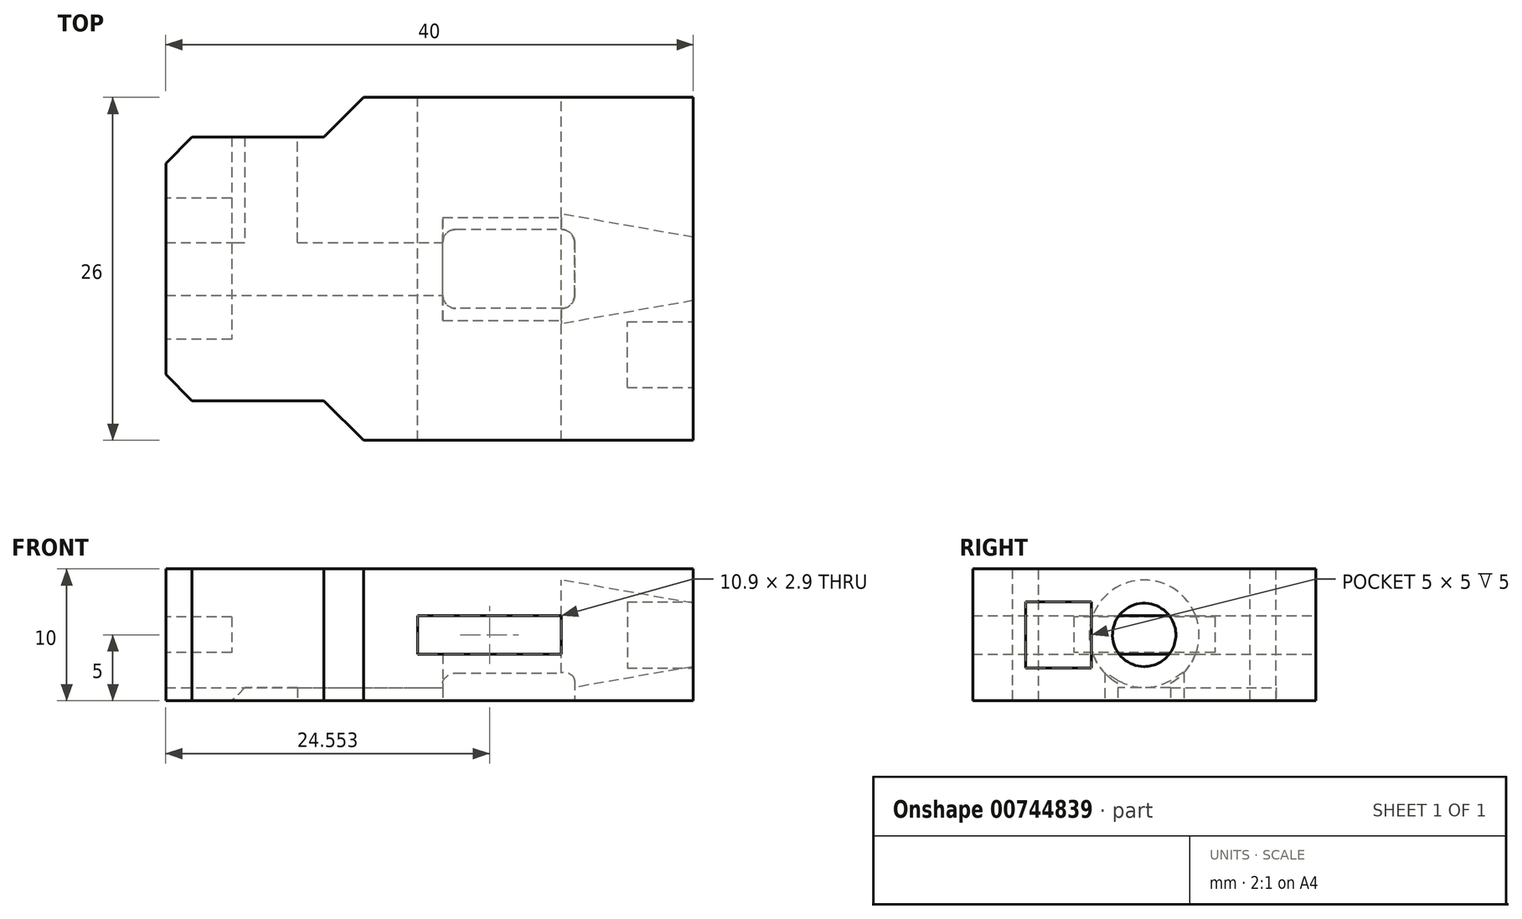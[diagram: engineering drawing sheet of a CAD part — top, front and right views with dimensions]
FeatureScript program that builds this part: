
annotation { "Feature Type Name" : "Feature", "Feature Type Description" : "" }
export const myFeature = defineFeature(function(context is Context, id is Id, definition is map)
    precondition{}
    {
        {
            var Q0;
            Q0=qCreatedBy(makeId("Top.planeOp"),FACE);
            var sketch = newSketch(context, id + "F0", { "sketchPlane" : qUnion([Q0])});
            skPoint(sketch, "E0", {"position": v(-7.73, 0) * mm});
            skLineSegment(sketch, "E1.bottom", {"start": v(-2.73, 10) * mm, "end": v(-12.73, 10) * mm});
            skLineSegment(sketch, "E1.top", {"start": v(-2.73, -10) * mm, "end": v(-12.73, -10) * mm});
            skLineSegment(sketch, "E1.left", {"start": v(-2.73, 10) * mm, "end": v(-2.73, -10) * mm});
            skLineSegment(sketch, "E1.right", {"start": v(-12.73, 10) * mm, "end": v(-12.73, -10) * mm});
            skLineSegment(sketch, "E2", {"start": v(-2.73, 10) * mm, "end": v(-2.73, 13) * mm});
            skLineSegment(sketch, "E3", {"start": v(-2.73, 13) * mm, "end": v(27.27, 13) * mm});
            skLineSegment(sketch, "E4", {"start": v(27.27, 13) * mm, "end": v(27.27, -13) * mm});
            skLineSegment(sketch, "E5", {"start": v(27.27, -13) * mm, "end": v(-2.73, -13) * mm});
            skLineSegment(sketch, "E6", {"start": v(-2.73, -13) * mm, "end": v(-2.73, -10) * mm});
            skSolve(sketch);
        }
        {
            var Q0;
            Q0=makeQuery(id+"F0.imprint","IMPRINT",FACE,{"disambiguationData":[TD([[makeQuery(id+"F0.imprint","IMPRINT",EDGE,{"derivedFrom":sQuery(id+"F0.wireOp",EDGE,"E1.bottom")}),1.0]])]});
            var Q1;
            Q1=makeQuery(id+"F0.imprint","IMPRINT",FACE,{"disambiguationData":[TD([[makeQuery(id+"F0.imprint","IMPRINT",EDGE,{"derivedFrom":sQuery(id+"F0.wireOp",EDGE,"E1.left")}),1.0]])]});
            extrude(context, id + "F1", {"entities" : qUnion([Q0, Q1]), "depth" : 10 * mm});
        }
        {
            var Q0;
            Q0=makeQuery(id+"F1.opExtrude","SWEPT_FACE",FACE,{"disambiguationData":[OSD([sQuery(id+"F0.wireOp",EDGE,"E1.right")])]});
            var sketch = newSketch(context, id + "F2", { "sketchPlane" : qUnion([Q0])});
            skLineSegment(sketch, "E7", {"start": v(-10, 10) * mm, "end": v(10, 0) * mm});
            skLineSegment(sketch, "E8", {"start": v(-10, 0) * mm, "end": v(10, 10) * mm});
            skLineSegment(sketch, "E9.bottom", {"start": v(-5.35, 6.35) * mm, "end": v(5.35, 6.35) * mm});
            skLineSegment(sketch, "E9.top", {"start": v(-5.35, 3.65) * mm, "end": v(5.35, 3.65) * mm});
            skLineSegment(sketch, "E9.left", {"start": v(-5.35, 6.35) * mm, "end": v(-5.35, 3.65) * mm});
            skLineSegment(sketch, "E9.right", {"start": v(5.35, 6.35) * mm, "end": v(5.35, 3.65) * mm});
            skPoint(sketch, "E9.middle", {"position": v(0, 5) * mm});
            skSolve(sketch);
        }
        {
            var Q0;
            {var subQ0=sQuery(id+"F2.wireOp",EDGE,"E9.left");Q0=makeQuery(id+"F2.imprint","IMPRINT",FACE,{"disambiguationData":[TD([[makeQuery(id+"F2.imprint","IMPRINT",EDGE,{"derivedFrom":subQ0}),1.0]])]});}
            var Q1;
            {var subQ0=sQuery(id+"F2.wireOp",EDGE,"E8");var subQ1=sQuery(id+"F2.wireOp",EDGE,"E7");var subQ2=makeQuery(id+"F2.imprint","INTERSECT",VERTEX,{"derivedFrom":[subQ1,subQ0]});Q1=makeQuery(id+"F2.imprint","IMPRINT",FACE,{"disambiguationData":[TD([[makeQuery(id+"F2.imprint","IMPRINT",EDGE,{"disambiguationData":[TD([[subQ2,-1.0]])],"derivedFrom":subQ1}),-1.0]])]});}
            var Q2;
            {var subQ0=sQuery(id+"F2.wireOp",EDGE,"E9.right");Q2=makeQuery(id+"F2.imprint","IMPRINT",FACE,{"disambiguationData":[TD([[makeQuery(id+"F2.imprint","IMPRINT",EDGE,{"derivedFrom":subQ0}),-1.0]])]});}
            var Q3;
            {var subQ0=sQuery(id+"F2.wireOp",EDGE,"E9.bottom");var subQ1=sQuery(id+"F2.wireOp",EDGE,"E7");var subQ2=makeQuery(id+"F2.imprint","INTERSECT",VERTEX,{"derivedFrom":[subQ1,subQ0]});Q3=makeQuery(id+"F2.imprint","IMPRINT",FACE,{"disambiguationData":[TD([[makeQuery(id+"F2.imprint","IMPRINT",EDGE,{"disambiguationData":[TD([[subQ2,-1.0]])],"derivedFrom":subQ1}),1.0]])]});}
            extrude(context, id + "F3", {"entities" : qUnion([Q0, Q1, Q2, Q3]), "operationType" : NewBodyOperationType.REMOVE, "oppositeDirection" : true, "depth" : 5 * mm});
        }
        {
            var Q0;
            Q0=makeQuery(id+"F1.opExtrude","SWEPT_EDGE",EDGE,{"disambiguationData":[OSD([sQuery(id+"F0.wireOp",EDGE,"E2"),sQuery(id+"F0.wireOp",EDGE,"E3")])]});
            var Q1;
            Q1=makeQuery(id+"F1.opExtrude","SWEPT_EDGE",EDGE,{"disambiguationData":[OSD([sQuery(id+"F0.wireOp",EDGE,"E5"),sQuery(id+"F0.wireOp",EDGE,"E6")])]});
            chamfer(context, id + "F4", {"entities" : qUnion([Q0, Q1]), "width" : 5 * mm, "tangentPropagation" : true});
        }
        {
            var Q0;
            Q0=makeQuery(id+"F1.opExtrude","SWEPT_EDGE",EDGE,{"disambiguationData":[OSD([sQuery(id+"F0.wireOp",EDGE,"E1.bottom"),sQuery(id+"F0.wireOp",EDGE,"E1.right")])]});
            var Q1;
            Q1=makeQuery(id+"F1.opExtrude","SWEPT_EDGE",EDGE,{"disambiguationData":[OSD([sQuery(id+"F0.wireOp",EDGE,"E1.top"),sQuery(id+"F0.wireOp",EDGE,"E1.right")])]});
            chamfer(context, id + "F5", {"entities" : qUnion([Q0, Q1]), "width" : 2 * mm, "tangentPropagation" : true});
        }
        {
            var Q0;
            Q0=makeQuery(id+"F1.opExtrude","SWEPT_FACE",FACE,{"disambiguationData":[OSD([sQuery(id+"F0.wireOp",EDGE,"E3")])]});
            var sketch = newSketch(context, id + "F6", { "sketchPlane" : qUnion([Q0])});
            skLineSegment(sketch, "E10", {"start": v(-27.27, 10) * mm, "end": v(-2.27, 0) * mm});
            skLineSegment(sketch, "E11", {"start": v(-2.27, 0) * mm, "end": v(-2.27, 10) * mm});
            skLineSegment(sketch, "E12", {"start": v(-2.27, 10) * mm, "end": v(-27.27, 0) * mm});
            skLineSegment(sketch, "E13", {"start": v(-14.77, 5) * mm, "end": v(-27.27, 5) * mm});
            skLineSegment(sketch, "E14", {"start": v(-14.77, 5) * mm, "end": v(-2.27, 5) * mm});
            skPoint(sketch, "E15", {"position": v(-17.27, 5) * mm});
            skLineSegment(sketch, "E16", {"start": v(-17.27, 5) * mm, "end": v(-17.27, 6.45) * mm});
            skLineSegment(sketch, "E17", {"start": v(-17.27, 6.45) * mm, "end": v(-6.37, 6.45) * mm});
            skLineSegment(sketch, "E18", {"start": v(-6.37, 6.45) * mm, "end": v(-6.37, 5) * mm});
            skLineSegment(sketch, "E19.MirrorCS", {"start": v(-17.27, 3.55) * mm, "end": v(-6.37, 3.55) * mm});
            skLineSegment(sketch, "E20.MirrorCS", {"start": v(-17.27, 5) * mm, "end": v(-17.27, 3.55) * mm});
            skLineSegment(sketch, "E21.MirrorCS", {"start": v(-6.37, 3.55) * mm, "end": v(-6.37, 5) * mm});
            skSolve(sketch);
        }
        {
            var Q0;
            {var subQ5=sQuery(id+"F6.wireOp",EDGE,"E16");Q0=makeQuery(id+"F6.imprint","IMPRINT",FACE,{"disambiguationData":[TD([[makeQuery(id+"F6.imprint","IMPRINT",EDGE,{"derivedFrom":subQ5}),-1.0]])]});}
            var Q1;
            {var subQ3=sQuery(id+"F6.wireOp",EDGE,"E17");var subQ5=sQuery(id+"F6.wireOp",EDGE,"E18");var subQ6=makeQuery(id+"F6.imprint","INTERSECT",VERTEX,{"derivedFrom":[subQ3,subQ5]});Q1=makeQuery(id+"F6.imprint","IMPRINT",FACE,{"disambiguationData":[TD([[makeQuery(id+"F6.imprint","IMPRINT",EDGE,{"disambiguationData":[TD([[subQ6,1.0]])],"derivedFrom":subQ3}),-1.0]])]});}
            var Q2;
            {var subQ5=sQuery(id+"F6.wireOp",EDGE,"E20.MirrorCS");Q2=makeQuery(id+"F6.imprint","IMPRINT",FACE,{"disambiguationData":[TD([[makeQuery(id+"F6.imprint","IMPRINT",EDGE,{"derivedFrom":subQ5}),1.0]])]});}
            var Q3;
            {var subQ3=sQuery(id+"F6.wireOp",EDGE,"E21.MirrorCS");var subQ5=sQuery(id+"F6.wireOp",EDGE,"E19.MirrorCS");var subQ6=makeQuery(id+"F6.imprint","INTERSECT",VERTEX,{"derivedFrom":[subQ5,subQ3]});Q3=makeQuery(id+"F6.imprint","IMPRINT",FACE,{"disambiguationData":[TD([[makeQuery(id+"F6.imprint","IMPRINT",EDGE,{"disambiguationData":[TD([[subQ6,1.0]])],"derivedFrom":subQ5}),1.0]])]});}
            var Q4;
            {var subQ1=sQuery(id+"F6.wireOp",EDGE,"E12");var subQ3=sQuery(id+"F6.wireOp",EDGE,"E18");var subQ4=makeQuery(id+"F6.imprint","INTERSECT",VERTEX,{"derivedFrom":[subQ1,subQ3]});Q4=makeQuery(id+"F6.imprint","IMPRINT",FACE,{"disambiguationData":[TD([[makeQuery(id+"F6.imprint","IMPRINT",EDGE,{"disambiguationData":[TD([[subQ4,-1.0]])],"derivedFrom":subQ3}),-1.0]])]});}
            var Q5;
            {var subQ1=sQuery(id+"F6.wireOp",EDGE,"E10");var subQ3=sQuery(id+"F6.wireOp",EDGE,"E21.MirrorCS");var subQ4=makeQuery(id+"F6.imprint","INTERSECT",VERTEX,{"derivedFrom":[subQ1,subQ3]});Q5=makeQuery(id+"F6.imprint","IMPRINT",FACE,{"disambiguationData":[TD([[makeQuery(id+"F6.imprint","IMPRINT",EDGE,{"disambiguationData":[TD([[subQ4,-1.0]])],"derivedFrom":subQ3}),1.0]])]});}
            var Q6;
            {var subQ1=sQuery(id+"F6.wireOp",EDGE,"E10");var subQ3=sQuery(id+"F6.wireOp",EDGE,"E19.MirrorCS");var subQ4=makeQuery(id+"F6.imprint","INTERSECT",VERTEX,{"derivedFrom":[subQ1,subQ3]});Q6=makeQuery(id+"F6.imprint","IMPRINT",FACE,{"disambiguationData":[TD([[makeQuery(id+"F6.imprint","IMPRINT",EDGE,{"disambiguationData":[TD([[subQ4,1.0]])],"derivedFrom":subQ3}),1.0]])]});}
            var Q7;
            {var subQ1=sQuery(id+"F6.wireOp",EDGE,"E10");var subQ3=sQuery(id+"F6.wireOp",EDGE,"E17");var subQ4=makeQuery(id+"F6.imprint","INTERSECT",VERTEX,{"derivedFrom":[subQ1,subQ3]});Q7=makeQuery(id+"F6.imprint","IMPRINT",FACE,{"disambiguationData":[TD([[makeQuery(id+"F6.imprint","IMPRINT",EDGE,{"disambiguationData":[TD([[subQ4,-1.0]])],"derivedFrom":subQ3}),-1.0]])]});}
            var Q8;
            Q8=makeQuery(id+"F1.opExtrude","SWEPT_FACE",FACE,{"disambiguationData":[OSD([sQuery(id+"F0.wireOp",EDGE,"E5")])]});
            extrude(context, id + "F7", {"entities" : qUnion([Q0, Q1, Q2, Q3, Q4, Q5, Q6, Q7]), "operationType" : NewBodyOperationType.REMOVE, "endBound" : BoundingType.UP_TO_SURFACE, "oppositeDirection" : true, "endBoundEntityFace" : qUnion([Q8]), "depth" : 25 * mm});
        }
        {
            var Q0;
            Q0=makeQuery(id+"F1.opExtrude","SWEPT_FACE",FACE,{"disambiguationData":[OSD([sQuery(id+"F0.wireOp",EDGE,"E4")])]});
            var sketch = newSketch(context, id + "F8", { "sketchPlane" : qUnion([Q0])});
            skLineSegment(sketch, "E22", {"start": v(13, 0) * mm, "end": v(-13, 10) * mm});
            skLineSegment(sketch, "E23", {"start": v(13, 10) * mm, "end": v(-13, 0) * mm});
            skPoint(sketch, "E24", {"position": v(0, 5) * mm});
            skCircle(sketch, "E25", {"center": v(0, 5) * mm, "radius": 2.4 * mm});
            skLineSegment(sketch, "E26", {"start": v(0, 5) * mm, "end": v(-13, 5) * mm});
            skPoint(sketch, "E27", {"position": v(-6.5, 5) * mm});
            skLineSegment(sketch, "E28.bottom", {"start": v(-9, 7.5) * mm, "end": v(-4, 7.5) * mm});
            skLineSegment(sketch, "E28.top", {"start": v(-9, 2.5) * mm, "end": v(-4, 2.5) * mm});
            skLineSegment(sketch, "E28.left", {"start": v(-9, 7.5) * mm, "end": v(-9, 2.5) * mm});
            skLineSegment(sketch, "E28.right", {"start": v(-4, 7.5) * mm, "end": v(-4, 2.5) * mm});
            skSolve(sketch);
        }
        {
            var Q0;
            {var subQ0=sQuery(id+"F8.wireOp",EDGE,"E23");var subQ1=sQuery(id+"F8.wireOp",EDGE,"E22");var subQ2=makeQuery(id+"F8.imprint","INTERSECT",VERTEX,{"derivedFrom":[subQ1,subQ0]});Q0=makeQuery(id+"F8.imprint","IMPRINT",FACE,{"disambiguationData":[TD([[makeQuery(id+"F8.imprint","IMPRINT",EDGE,{"disambiguationData":[TD([[subQ2,-1.0]])],"derivedFrom":subQ1}),1.0]])]});}
            var Q1;
            {var subQ0=sQuery(id+"F8.wireOp",EDGE,"E23");var subQ1=sQuery(id+"F8.wireOp",EDGE,"E22");var subQ2=makeQuery(id+"F8.imprint","INTERSECT",VERTEX,{"derivedFrom":[subQ1,subQ0]});Q1=makeQuery(id+"F8.imprint","IMPRINT",FACE,{"disambiguationData":[TD([[makeQuery(id+"F8.imprint","IMPRINT",EDGE,{"disambiguationData":[TD([[subQ2,-1.0]])],"derivedFrom":subQ1}),-1.0]])]});}
            var Q2;
            {var subQ0=sQuery(id+"F8.wireOp",EDGE,"E25");var subQ1=sQuery(id+"F8.wireOp",EDGE,"E22");var subQ2=makeQuery(id+"F8.imprint","INTERSECT",VERTEX,{"disambiguationData":[OD(0.0)],"derivedFrom":[subQ1,subQ0]});Q2=makeQuery(id+"F8.imprint","IMPRINT",FACE,{"disambiguationData":[TD([[makeQuery(id+"F8.imprint","IMPRINT",EDGE,{"disambiguationData":[TD([[subQ2,-1.0]])],"derivedFrom":subQ1}),-1.0]])]});}
            var Q3;
            {var subQ0=sQuery(id+"F8.wireOp",EDGE,"E25");var subQ1=sQuery(id+"F8.wireOp",EDGE,"E22");var subQ2=makeQuery(id+"F8.imprint","INTERSECT",VERTEX,{"disambiguationData":[OD(0.0)],"derivedFrom":[subQ1,subQ0]});Q3=makeQuery(id+"F8.imprint","IMPRINT",FACE,{"disambiguationData":[TD([[makeQuery(id+"F8.imprint","IMPRINT",EDGE,{"disambiguationData":[TD([[subQ2,-1.0]])],"derivedFrom":subQ1}),1.0]])]});}
            var Q4;
            {var subQ1=sQuery(id+"F8.wireOp",EDGE,"E23");var subQ3=sQuery(id+"F8.wireOp",EDGE,"E25");var subQ4=makeQuery(id+"F8.imprint","INTERSECT",VERTEX,{"disambiguationData":[OD(1.0)],"derivedFrom":[subQ1,subQ3]});Q4=makeQuery(id+"F8.imprint","IMPRINT",FACE,{"disambiguationData":[TD([[makeQuery(id+"F8.imprint","IMPRINT",EDGE,{"disambiguationData":[TD([[subQ4,1.0]])],"derivedFrom":subQ3}),1.0]])]});}
            var Q5;
            Q5=makeQuery(id+"F7.boolean.opBoolean","COPY",FACE,{"derivedFrom":makeQuery(id+"F7.opExtrude","SWEPT_FACE",FACE,{"disambiguationData":[OSD([sQuery(id+"F6.wireOp",EDGE,"E16"),sQuery(id+"F6.wireOp",EDGE,"E20.MirrorCS")])]})});
            extrude(context, id + "F9", {"entities" : qUnion([Q0, Q1, Q2, Q3, Q4]), "operationType" : NewBodyOperationType.REMOVE, "endBound" : BoundingType.UP_TO_SURFACE, "oppositeDirection" : true, "endBoundEntityFace" : qUnion([Q5]), "depth" : 25 * mm, "hasDraft" : true, "draftAngle" : 10 * degree});
        }
        {
            var Q0;
            Q0=makeQuery(id+"F1.opExtrude","CAP_FACE",FACE,{"disambiguationData":[OSD([sQuery(id+"F0.wireOp",EDGE,"E1.bottom"),sQuery(id+"F0.wireOp",EDGE,"E1.top"),sQuery(id+"F0.wireOp",EDGE,"E1.right"),sQuery(id+"F0.wireOp",EDGE,"E2"),sQuery(id+"F0.wireOp",EDGE,"E3"),sQuery(id+"F0.wireOp",EDGE,"E4"),sQuery(id+"F0.wireOp",EDGE,"E5"),sQuery(id+"F0.wireOp",EDGE,"E6")])],"isStart":true});
            var sketch = newSketch(context, id + "F10", { "sketchPlane" : qUnion([Q0])});
            skPoint(sketch, "E29", {"position": v(17.27, 0) * mm});
            skLineSegment(sketch, "E30.bottom", {"start": v(18.27, 3) * mm, "end": v(16.27, 3) * mm});
            skLineSegment(sketch, "E30.top", {"start": v(18.27, -3) * mm, "end": v(16.27, -3) * mm});
            skLineSegment(sketch, "E30.left", {"start": v(18.27, 3) * mm, "end": v(18.27, -3) * mm});
            skLineSegment(sketch, "E31", {"start": v(18.27, 3) * mm, "end": v(8.27, 3) * mm});
            skLineSegment(sketch, "E32", {"start": v(8.27, 3) * mm, "end": v(8.27, -3) * mm});
            skLineSegment(sketch, "E33", {"start": v(8.27, -3) * mm, "end": v(18.27, -3) * mm});
            skSolve(sketch);
        }
        {
            var Q0;
            Q0=qSketchRegion(id+"F10",true);
            extrude(context, id + "F11", {"entities" : qUnion([Q0]), "operationType" : NewBodyOperationType.REMOVE, "oppositeDirection" : true, "depth" : 5 * mm});
        }
        {
            var Q0;
            {var subQ1=makeQuery(id+"F7.boolean.opBoolean","COPY",FACE,{"derivedFrom":makeQuery(id+"F7.opExtrude","SWEPT_FACE",FACE,{"disambiguationData":[OSD([sQuery(id+"F6.wireOp",EDGE,"E19.MirrorCS")])]})});var subQ2=sQuery(id+"F8.wireOp",EDGE,"E25");Q0=makeQuery(id+"F11.boolean.opBoolean","SPLIT",FACE,{"disambiguationData":[TD([makeQuery(id+"F11.opExtrude","SWEPT_FACE",FACE,{"disambiguationData":[OSD([sQuery(id+"F10.wireOp",EDGE,"E33")])]})])],"derivedFrom":makeQuery(id+"F9.boolean.opBoolean","COPY",FACE,{"disambiguationData":[TD([subQ1])],"derivedFrom":makeQuery(id+"F9.opExtrude","CAP_FACE",FACE,{"disambiguationData":[OSD([subQ2])],"isStart":false})})});}
            var Q1;
            {var subQ1=makeQuery(id+"F7.boolean.opBoolean","COPY",FACE,{"derivedFrom":makeQuery(id+"F7.opExtrude","SWEPT_FACE",FACE,{"disambiguationData":[OSD([sQuery(id+"F6.wireOp",EDGE,"E19.MirrorCS")])]})});var subQ2=sQuery(id+"F8.wireOp",EDGE,"E25");Q1=makeQuery(id+"F11.boolean.opBoolean","SPLIT",FACE,{"disambiguationData":[TD([makeQuery(id+"F11.opExtrude","SWEPT_FACE",FACE,{"disambiguationData":[OSD([sQuery(id+"F10.wireOp",EDGE,"E31")])]})])],"derivedFrom":makeQuery(id+"F9.boolean.opBoolean","COPY",FACE,{"disambiguationData":[TD([subQ1])],"derivedFrom":makeQuery(id+"F9.opExtrude","CAP_FACE",FACE,{"disambiguationData":[OSD([subQ2])],"isStart":false})})});}
            var Q2;
            Q2=makeQuery(id+"F11.boolean.opBoolean","COPY",FACE,{"derivedFrom":makeQuery(id+"F11.opExtrude","SWEPT_FACE",FACE,{"disambiguationData":[OSD([sQuery(id+"F10.wireOp",EDGE,"E32")])]})});
            extrude(context, id + "F12", {"entities" : qUnion([Q0, Q1]), "operationType" : NewBodyOperationType.REMOVE, "endBound" : BoundingType.UP_TO_SURFACE, "oppositeDirection" : true, "endBoundEntityFace" : qUnion([Q2]), "depth" : 4.47 * mm});
        }
        {
            var Q0;
            Q0=makeQuery(id+"F11.boolean.opBoolean","COPY",EDGE,{"derivedFrom":makeQuery(id+"F11.opExtrude","SWEPT_EDGE",EDGE,{"disambiguationData":[OSD([sQuery(id+"F10.wireOp",EDGE,"E30.left"),sQuery(id+"F10.wireOp",EDGE,"E31")])]})});
            var Q1;
            Q1=makeQuery(id+"F11.boolean.opBoolean","COPY",EDGE,{"derivedFrom":makeQuery(id+"F11.opExtrude","SWEPT_EDGE",EDGE,{"disambiguationData":[OSD([sQuery(id+"F10.wireOp",EDGE,"E31"),sQuery(id+"F10.wireOp",EDGE,"E32")])]})});
            var Q2;
            Q2=makeQuery(id+"F11.boolean.opBoolean","COPY",EDGE,{"derivedFrom":makeQuery(id+"F11.opExtrude","SWEPT_EDGE",EDGE,{"disambiguationData":[OSD([sQuery(id+"F10.wireOp",EDGE,"E32"),sQuery(id+"F10.wireOp",EDGE,"E33")])]})});
            var Q3;
            Q3=makeQuery(id+"F11.boolean.opBoolean","COPY",EDGE,{"derivedFrom":makeQuery(id+"F11.opExtrude","SWEPT_EDGE",EDGE,{"disambiguationData":[OSD([sQuery(id+"F10.wireOp",EDGE,"E30.left"),sQuery(id+"F10.wireOp",EDGE,"E33")])]})});
            fillet(context, id + "F13", {"entities" : qUnion([Q0, Q1, Q2, Q3]), "radius" : 1 * mm, "tangentPropagation" : true, "allowEdgeOverflow" : false});
        }
        {
            var Q0;
            Q0=makeQuery(id+"F1.opExtrude","CAP_FACE",FACE,{"disambiguationData":[OSD([sQuery(id+"F0.wireOp",EDGE,"E1.bottom"),sQuery(id+"F0.wireOp",EDGE,"E1.top"),sQuery(id+"F0.wireOp",EDGE,"E1.right"),sQuery(id+"F0.wireOp",EDGE,"E2"),sQuery(id+"F0.wireOp",EDGE,"E3"),sQuery(id+"F0.wireOp",EDGE,"E4"),sQuery(id+"F0.wireOp",EDGE,"E5"),sQuery(id+"F0.wireOp",EDGE,"E6")])],"isStart":true});
            var sketch = newSketch(context, id + "F14", { "sketchPlane" : qUnion([Q0])});
            skLineSegment(sketch, "E34.bottom", {"start": v(-12.73, 2) * mm, "end": v(18.27, 2) * mm});
            skLineSegment(sketch, "E34.top", {"start": v(-12.73, -2) * mm, "end": v(18.27, -2) * mm});
            skLineSegment(sketch, "E34.left", {"start": v(-12.73, 2) * mm, "end": v(-12.73, -2) * mm});
            skLineSegment(sketch, "E34.right", {"start": v(18.27, 2) * mm, "end": v(18.27, -2) * mm});
            skLineSegment(sketch, "E35.bottom", {"start": v(-12.73, -2) * mm, "end": v(-2.73, -2) * mm});
            skLineSegment(sketch, "E35.top", {"start": v(-6.73, -10) * mm, "end": v(-2.73, -10) * mm});
            skLineSegment(sketch, "E35.right", {"start": v(-2.73, -2) * mm, "end": v(-2.73, -10) * mm});
            skLineSegment(sketch, "E36", {"start": v(-6.73, -10) * mm, "end": v(-6.73, -2) * mm});
            skSolve(sketch);
        }
        {
            var Q0;
            {var subQ1=sQuery(id+"F14.wireOp",EDGE,"E34.left");Q0=makeQuery(id+"F14.imprint","IMPRINT",FACE,{"disambiguationData":[TD([[makeQuery(id+"F14.imprint","IMPRINT",EDGE,{"derivedFrom":subQ1}),-1.0]])]});}
            var Q1;
            Q1=makeQuery(id+"F14.imprint","IMPRINT",FACE,{"disambiguationData":[TD([[makeQuery(id+"F14.imprint","IMPRINT",EDGE,{"derivedFrom":sQuery(id+"F14.wireOp",EDGE,"E35.top")}),-1.0]])]});
            extrude(context, id + "F15", {"entities" : qUnion([Q0, Q1]), "operationType" : NewBodyOperationType.REMOVE, "oppositeDirection" : true, "depth" : 1 * mm});
        }
        {
            var Q0;
            Q0=makeQuery(id+"F15.boolean.opBoolean","COPY",EDGE,{"derivedFrom":makeQuery(id+"F15.opExtrude","CAP_EDGE",EDGE,{"disambiguationData":[OSD([sQuery(id+"F14.wireOp",EDGE,"E36")])],"isStart":true})});
            chamfer(context, id + "F16", {"entities" : qUnion([Q0]), "width" : 1 * mm, "tangentPropagation" : true});
        }
        {
            var Q0;
            {var subQ0=sQuery(id+"F8.wireOp",EDGE,"E28.right");var subQ1=sQuery(id+"F8.wireOp",EDGE,"E22");var subQ2=makeQuery(id+"F8.imprint","INTERSECT",VERTEX,{"derivedFrom":[subQ1,subQ0]});Q0=makeQuery(id+"F8.imprint","IMPRINT",FACE,{"disambiguationData":[TD([[makeQuery(id+"F8.imprint","IMPRINT",EDGE,{"disambiguationData":[TD([[subQ2,-1.0]])],"derivedFrom":subQ1}),-1.0]])]});}
            var Q1;
            {var subQ5=sQuery(id+"F8.wireOp",EDGE,"E22");var subQ7=sQuery(id+"F8.wireOp",EDGE,"E28.right");var subQ9=makeQuery(id+"F8.imprint","INTERSECT",VERTEX,{"derivedFrom":[subQ5,subQ7]});Q1=makeQuery(id+"F8.imprint","IMPRINT",FACE,{"disambiguationData":[TD([[makeQuery(id+"F8.imprint","IMPRINT",EDGE,{"disambiguationData":[TD([[subQ9,-1.0]])],"derivedFrom":subQ5}),1.0]])]});}
            var Q2;
            {var subQ5=sQuery(id+"F8.wireOp",EDGE,"E23");var subQ7=sQuery(id+"F8.wireOp",EDGE,"E28.right");var subQ9=makeQuery(id+"F8.imprint","INTERSECT",VERTEX,{"derivedFrom":[subQ5,subQ7]});Q2=makeQuery(id+"F8.imprint","IMPRINT",FACE,{"disambiguationData":[TD([[makeQuery(id+"F8.imprint","IMPRINT",EDGE,{"disambiguationData":[TD([[subQ9,-1.0]])],"derivedFrom":subQ5}),-1.0]])]});}
            var Q3;
            {var subQ0=sQuery(id+"F8.wireOp",EDGE,"E28.right");var subQ1=sQuery(id+"F8.wireOp",EDGE,"E23");var subQ2=makeQuery(id+"F8.imprint","INTERSECT",VERTEX,{"derivedFrom":[subQ1,subQ0]});Q3=makeQuery(id+"F8.imprint","IMPRINT",FACE,{"disambiguationData":[TD([[makeQuery(id+"F8.imprint","IMPRINT",EDGE,{"disambiguationData":[TD([[subQ2,-1.0]])],"derivedFrom":subQ1}),1.0]])]});}
            extrude(context, id + "F17", {"entities" : qUnion([Q0, Q1, Q2, Q3]), "operationType" : NewBodyOperationType.REMOVE, "oppositeDirection" : true, "depth" : 5 * mm});
        }
    });
